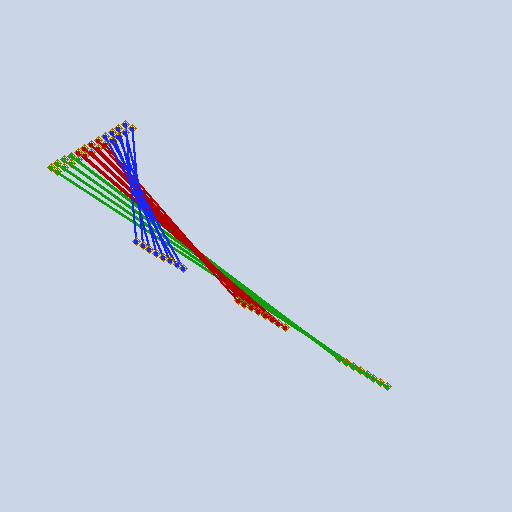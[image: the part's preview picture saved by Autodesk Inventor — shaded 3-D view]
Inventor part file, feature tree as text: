
AUTODESK INVENTOR PART (.ipt)
format: ipt  version: 2023.1 (Build 271208000, 208)  size: 217,088 bytes
history: native  units: mm (DEFAULTED — no unit token found)
features: other x96, plane x24, sketch x24, sweep x24
ambient origin geometry x8: Origin, YZ Plane, XZ Plane, XY Plane, X Axis, Y Axis, Z Axis, Center Point
feature tree (168):
  other  "Work Point1"
  other  "Work Point2"
  other  "Wire1"
  other  "Work Point3"
  other  "Work Point4"
  other  "Wire2"
  other  "Work Point5"
  other  "Work Point6"
  other  "Wire3"
  other  "Work Point7"
  other  "Work Point8"
  other  "Wire4"
  other  "Work Point9"
  other  "Work Point10"
  other  "Wire5"
  other  "Work Point11"
  other  "Work Point12"
  other  "Wire6"
  other  "Work Point13"
  other  "Work Point14"
  other  "Wire7"
  other  "Work Point15"
  other  "Work Point16"
  other  "Wire8"
  other  "Work Point17"
  other  "Work Point18"
  other  "Wire9"
  other  "Work Point19"
  other  "Work Point20"
  other  "Wire10"
  other  "Work Point21"
  other  "Work Point22"
  other  "Wire11"
  other  "Work Point23"
  other  "Work Point24"
  other  "Wire12"
  other  "Work Point25"
  other  "Work Point26"
  other  "Wire13"
  other  "Work Point27"
  other  "Work Point28"
  other  "Wire14"
  other  "Work Point29"
  other  "Work Point30"
  other  "Wire15"
  other  "Work Point31"
  other  "Work Point32"
  other  "Wire16"
  other  "Work Point33"
  other  "Work Point34"
  other  "Wire17"
  other  "Work Point35"
  other  "Work Point36"
  other  "Wire18"
  other  "Work Point37"
  other  "Work Point38"
  other  "Wire19"
  other  "Work Point39"
  other  "Work Point40"
  other  "Wire20"
  other  "Work Point41"
  other  "Work Point42"
  other  "Wire21"
  other  "Work Point43"
  other  "Work Point44"
  other  "Wire22"
  other  "Work Point45"
  other  "Work Point46"
  other  "Wire23"
  other  "Work Point47"
  other  "Work Point48"
  other  "Wire24"
  plane  "Work Plane1"
  plane  "Work Plane2"
  plane  "Work Plane3"
  plane  "Work Plane4"
  plane  "Work Plane5"
  plane  "Work Plane6"
  plane  "Work Plane7"
  plane  "Work Plane8"
  plane  "Work Plane9"
  plane  "Work Plane10"
  plane  "Work Plane11"
  plane  "Work Plane12"
  plane  "Work Plane13"
  plane  "Work Plane14"
  plane  "Work Plane15"
  plane  "Work Plane16"
  plane  "Work Plane17"
  plane  "Work Plane18"
  plane  "Work Plane19"
  plane  "Work Plane20"
  plane  "Work Plane21"
  plane  "Work Plane22"
  plane  "Work Plane23"
  plane  "Work Plane24"
  sketch  "Sketch1"  dims[d0=0.0mm d1=0.0mm d2=0.0mm d3=0.0mm]
  other  "Srf1"
  sketch  "Sketch2"  dims[d4=0.0mm d5=0.0mm d6=0.0mm d7=0.0mm]
  other  "Srf2"
  sketch  "Sketch3"  dims[d8=0.0mm d9=0.0mm d10=0.0mm d11=0.0mm]
  other  "Srf3"
  sketch  "Sketch4"  dims[d12=0.0mm d13=0.0mm d14=0.0mm d15=0.0mm]
  other  "Srf4"
  sketch  "Sketch5"  dims[d16=0.0mm d17=0.0mm d18=0.0mm d19=0.0mm]
  other  "Srf5"
  sketch  "Sketch6"  dims[d20=0.0mm d21=0.0mm d22=0.0mm d23=0.0mm]
  other  "Srf6"
  sketch  "Sketch7"  dims[d24=0.0mm d25=0.0mm d26=0.0mm d27=0.0mm]
  other  "Srf7"
  sketch  "Sketch8"  dims[d28=0.0mm d29=0.0mm d30=0.0mm d31=0.0mm]
  other  "Srf8"
  sketch  "Sketch9"  dims[d32=0.0mm d33=0.0mm d34=0.0mm d35=0.0mm]
  other  "Srf9"
  sketch  "Sketch10"  dims[d36=0.0mm d37=0.0mm d38=0.0mm d39=0.0mm]
  other  "Srf10"
  sketch  "Sketch11"  dims[d40=0.0mm d41=0.0mm d42=0.0mm d43=0.0mm]
  other  "Srf11"
  sketch  "Sketch12"  dims[d44=0.0mm d45=0.0mm d46=0.0mm d47=0.0mm]
  other  "Srf12"
  sketch  "Sketch13"
  other  "Srf13"
  sketch  "Sketch14"
  other  "Srf14"
  sketch  "Sketch15"
  other  "Srf15"
  sketch  "Sketch16"
  other  "Srf16"
  sketch  "Sketch17"
  other  "Srf17"
  sketch  "Sketch18"
  other  "Srf18"
  sketch  "Sketch19"
  other  "Srf19"
  sketch  "Sketch20"
  other  "Srf20"
  sketch  "Sketch21"
  other  "Srf21"
  sketch  "Sketch22"
  other  "Srf22"
  sketch  "Sketch23"
  other  "Srf23"
  sketch  "Sketch24"
  other  "Srf24"
  sweep  "SweepSrf1"
  sweep  "SweepSrf2"
  sweep  "SweepSrf3"
  sweep  "SweepSrf4"
  sweep  "SweepSrf5"
  sweep  "SweepSrf6"
  sweep  "SweepSrf7"
  sweep  "SweepSrf8"
  sweep  "SweepSrf9"
  sweep  "SweepSrf10"
  sweep  "SweepSrf11"
  sweep  "SweepSrf12"
  sweep  "SweepSrf13"
  sweep  "SweepSrf14"
  sweep  "SweepSrf15"
  sweep  "SweepSrf16"
  sweep  "SweepSrf17"
  sweep  "SweepSrf18"
  sweep  "SweepSrf19"
  sweep  "SweepSrf20"
  sweep  "SweepSrf21"
  sweep  "SweepSrf22"
  sweep  "SweepSrf23"
  sweep  "SweepSrf24"
